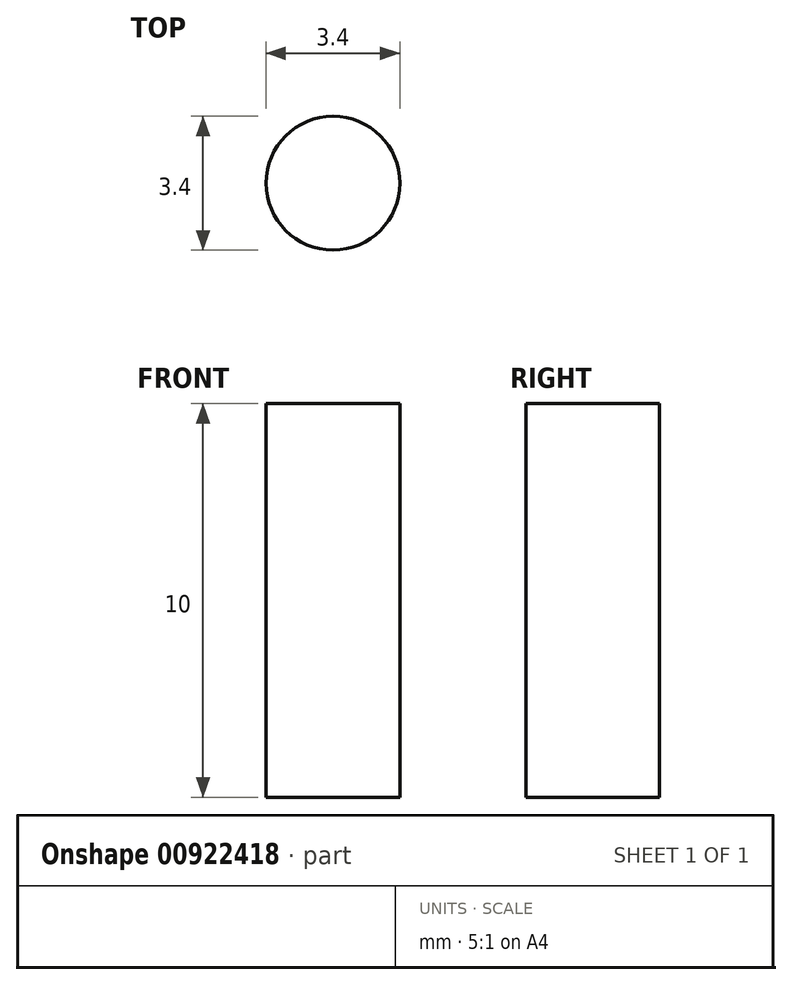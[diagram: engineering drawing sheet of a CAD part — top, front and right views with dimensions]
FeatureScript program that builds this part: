
annotation { "Feature Type Name" : "Feature", "Feature Type Description" : "" }
export const myFeature = defineFeature(function(context is Context, id is Id, definition is map)
    precondition{}
    {
        {
            var Q0;
            Q0=qCreatedBy(makeId("Top.planeOp"),FACE);
            var sketch = newSketch(context, id + "F0", { "sketchPlane" : qUnion([Q0])});
            skCircle(sketch, "E0", {"center": v(0, 0) * mm, "radius": 1.7 * mm});
            skSolve(sketch);
        }
        {
            var Q0;
            Q0 = qSketchRegion(id + "F0", true);
            extrude(context, id + "F1", {"entities" : qUnion([Q0]), "depth" : 10 * mm, "offsetDistance" : 25 * mm});
        }
    });
